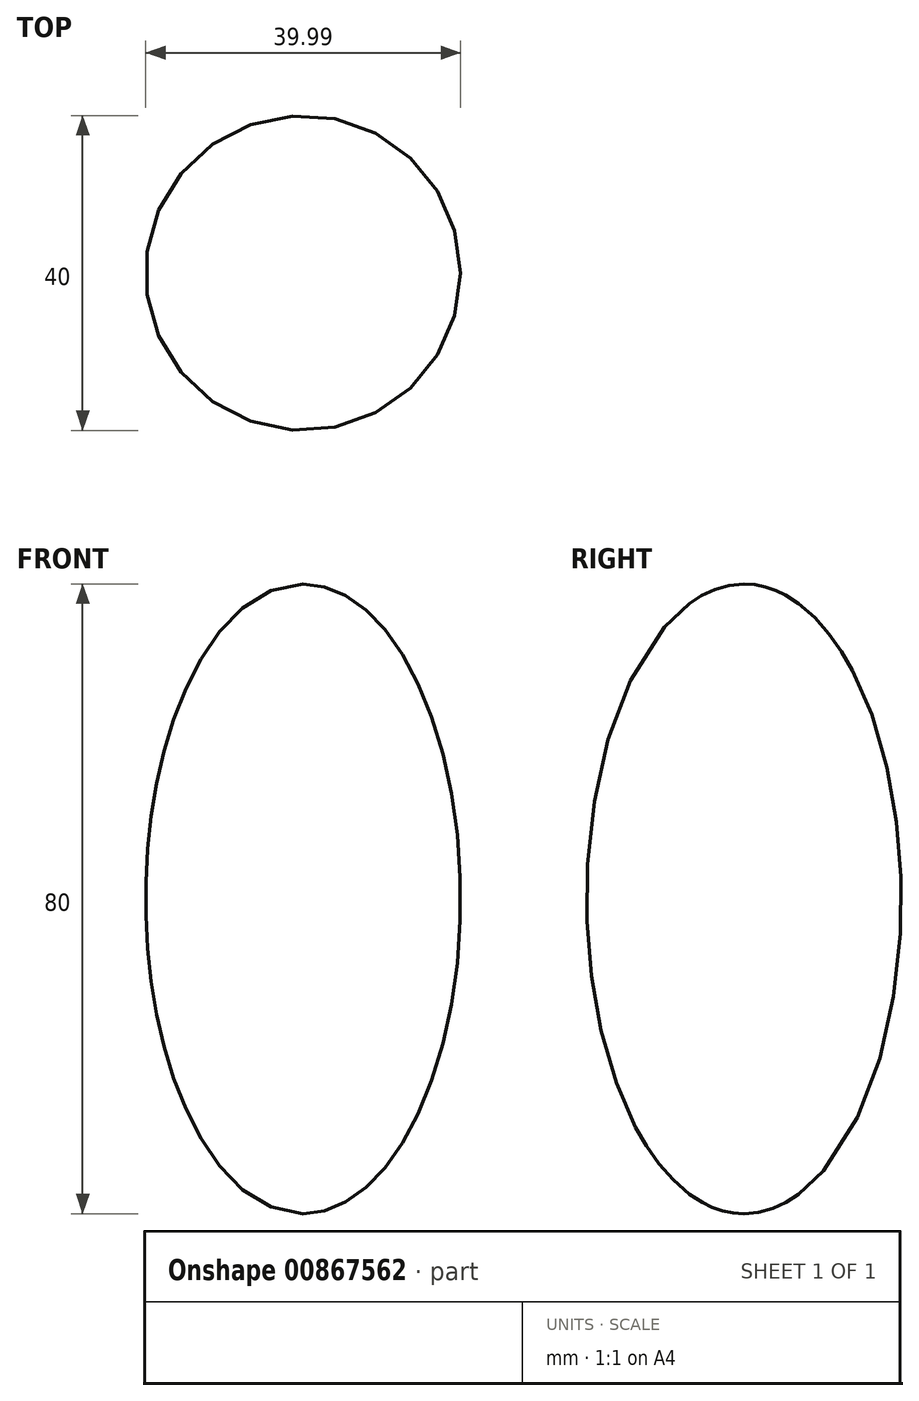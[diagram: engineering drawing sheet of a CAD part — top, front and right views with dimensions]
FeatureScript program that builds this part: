
annotation { "Feature Type Name" : "Feature", "Feature Type Description" : "" }
export const myFeature = defineFeature(function(context is Context, id is Id, definition is map)
    precondition{}
    {
        {
            var Q0;
            Q0=qCreatedBy(makeId("Front.planeOp"),FACE);
            var sketch = newSketch(context, id + "F0", { "sketchPlane" : qUnion([Q0])});
            skEllipticalArc(sketch, "E0", {});
            skLineSegment(sketch, "E1", {"start": v(0, 40) * mm, "end": v(0, -40) * mm});
            const initialGuessF0  = {"E0": [0, 0, 0, 1, 0.04, 0.02, 3.141592653589793, 0]};
            skSetInitialGuess(sketch, initialGuessF0);
            skSolve(sketch);
        }
        {
            var Q0;
            Q0 = qSketchRegion(id + "F0", true);
            var Q1;
            Q1=sQuery(id+"F0.wireOp",EDGE,"E1");
            revolve(context, id + "F1", {"surfaceOperationType" : NewSurfaceOperationType.NEW, "entities" : qUnion([Q0]), "axis" : qUnion([Q1]), "revolveType" : RevolveType.FULL});
        }
    });
